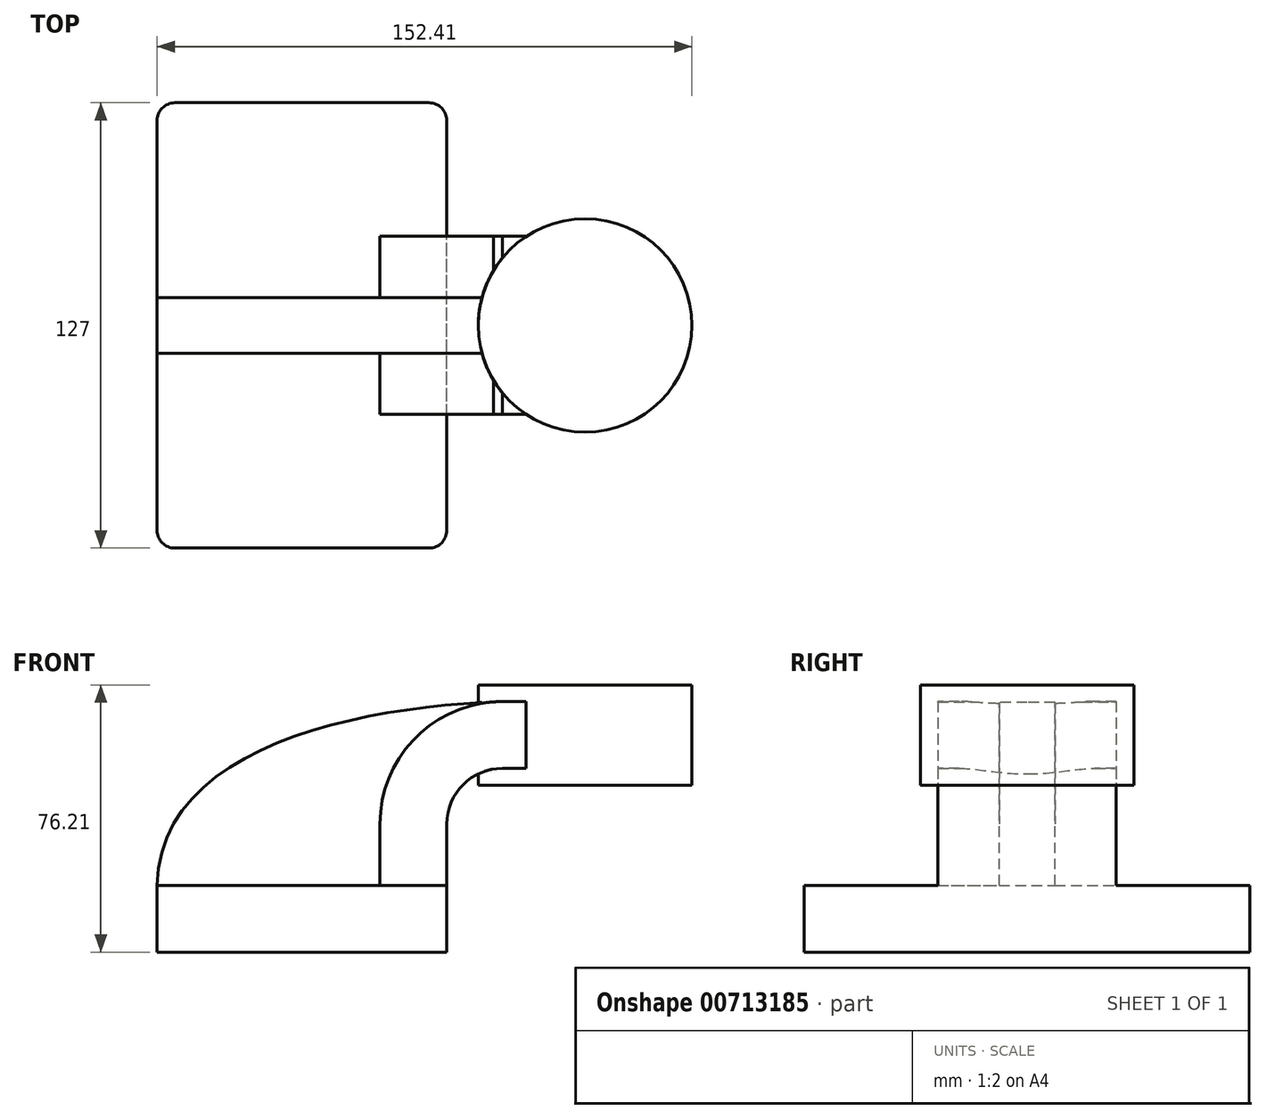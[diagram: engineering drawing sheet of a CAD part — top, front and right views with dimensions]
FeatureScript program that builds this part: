
annotation { "Feature Type Name" : "Feature", "Feature Type Description" : "" }
export const myFeature = defineFeature(function(context is Context, id is Id, definition is map)
    precondition{}
    {
        {
            var Q0;
            Q0=qCreatedBy(makeId("Front.planeOp"),FACE);
            var sketch = newSketch(context, id + "F0", { "sketchPlane" : qUnion([Q0])});
            skLineSegment(sketch, "E0.bottom", {"start": v(-41.28, 9.52) * mm, "end": v(41.28, 9.53) * mm});
            skLineSegment(sketch, "E0.top", {"start": v(-41.28, -9.53) * mm, "end": v(41.28, -9.53) * mm});
            skLineSegment(sketch, "E0.left", {"start": v(-41.28, 9.52) * mm, "end": v(-41.27, -9.53) * mm});
            skLineSegment(sketch, "E0.right", {"start": v(41.28, 9.53) * mm, "end": v(41.28, -9.52) * mm});
            skPoint(sketch, "E0.middle", {"position": v(0, 0) * mm});
            skLineSegment(sketch, "E1.bottom", {"start": v(111.12, 38.1) * mm, "end": v(60.33, 38.1) * mm});
            skLineSegment(sketch, "E1.top", {"start": v(111.12, 66.68) * mm, "end": v(60.33, 66.68) * mm});
            skLineSegment(sketch, "E1.left", {"start": v(111.12, 38.1) * mm, "end": v(111.12, 66.68) * mm});
            skLineSegment(sketch, "E1.right", {"start": v(60.33, 38.1) * mm, "end": v(60.33, 66.68) * mm});
            skPoint(sketch, "E1.middle", {"position": v(85.73, 52.39) * mm});
            skLineSegment(sketch, "E2", {"start": v(41.27, 9.53) * mm, "end": v(41.27, 27) * mm});
            skArc(sketch, "E3", {"start": v(57.15, 42.88) * mm, "mid": v(45.92, 38.23) * mm, "end": v(41.27, 27) * mm});
            skLineSegment(sketch, "E4", {"start": v(57.15, 42.88) * mm, "end": v(80.68, 42.88) * mm});
            skLineSegment(sketch, "E5.0", {"start": v(22.23, 9.53) * mm, "end": v(22.23, 27) * mm});
            skArc(sketch, "E5.1", {"start": v(57.15, 61.93) * mm, "mid": v(32.45, 51.7) * mm, "end": v(22.22, 27) * mm});
            skLineSegment(sketch, "E5.2", {"start": v(57.15, 61.93) * mm, "end": v(80.68, 61.93) * mm});
            skLineSegment(sketch, "E6", {"start": v(80.68, 38.1) * mm, "end": v(80.68, 66.68) * mm});
            skFitSpline(sketch, "E7", {"points": [v(-41.28, 9.53) * mm, v(57.15, 61.93) * mm], "startDerivative": vector(2.15, 119.8) * mm, "endDerivative": vector(119.5, 3.82) * mm});
            skSolve(sketch);
        }
        {
            var Q0;
            Q0=makeQuery(id+"F0.imprint","IMPRINT",FACE,{"disambiguationData":[TD([[makeQuery(id+"F0.imprint","IMPRINT",EDGE,{"derivedFrom":sQuery(id+"F0.wireOp",EDGE,"E0.top")}),1.0]])]});
            extrude(context, id + "F1", {"entities" : qUnion([Q0]), "endBound" : BoundingType.SYMMETRIC, "depth" : 127 * mm, "offsetDistance" : 25.4 * mm});
        }
        {
            var Q0;
            {var subQ1=sQuery(id+"F0.wireOp",EDGE,"E2");Q0=makeQuery(id+"F0.imprint","IMPRINT",FACE,{"disambiguationData":[TD([[makeQuery(id+"F0.imprint","IMPRINT",EDGE,{"derivedFrom":subQ1}),1.0]])]});}
            extrude(context, id + "F2", {"entities" : qUnion([Q0]), "operationType" : NewBodyOperationType.ADD, "endBound" : BoundingType.SYMMETRIC, "depth" : 50.8 * mm, "offsetDistance" : 25.4 * mm});
        }
        {
            var Q0;
            {var subQ3=sQuery(id+"F0.wireOp",EDGE,"E5.0");Q0=makeQuery(id+"F0.imprint","IMPRINT",FACE,{"disambiguationData":[TD([[makeQuery(id+"F0.imprint","IMPRINT",EDGE,{"derivedFrom":subQ3}),1.0]])]});}
            extrude(context, id + "F3", {"entities" : qUnion([Q0]), "operationType" : NewBodyOperationType.ADD, "endBound" : BoundingType.SYMMETRIC, "depth" : 15.88 * mm, "offsetDistance" : 25.4 * mm});
        }
        {
            var Q0;
            Q0=makeQuery(id+"F2.opExtrude","SWEPT_FACE",FACE,{"disambiguationData":[OSD([sQuery(id+"F0.wireOp",EDGE,"E1.right")])]});
            extrude(context, id + "F4", {"entities" : qUnion([Q0]), "operationType" : NewBodyOperationType.ADD, "depth" : 25.4 * mm, "offsetDistance" : 25.4 * mm});
        }
        {
            var Q0;
            {var subQ0=sQuery(id+"F0.wireOp",EDGE,"E1.left");Q0=makeQuery(id+"F0.imprint","IMPRINT",FACE,{"disambiguationData":[TD([[makeQuery(id+"F0.imprint","IMPRINT",EDGE,{"derivedFrom":subQ0}),1.0]])]});}
            var Q1;
            Q1=sQuery(id+"F0.wireOp",EDGE,"E6");
            revolve(context, id + "F5", {"operationType" : NewBodyOperationType.ADD, "surfaceOperationType" : NewSurfaceOperationType.NEW, "entities" : qUnion([Q0]), "axis" : qUnion([Q1]), "revolveType" : RevolveType.FULL});
        }
        {
            var Q0;
            Q0=makeQuery(id+"F1.opExtrude","CAP_EDGE",EDGE,{"disambiguationData":[OSD([sQuery(id+"F0.wireOp",EDGE,"E0.left")])],"isStart":true});
            var Q1;
            Q1=makeQuery(id+"F1.opExtrude","CAP_EDGE",EDGE,{"disambiguationData":[OSD([sQuery(id+"F0.wireOp",EDGE,"E0.left")])],"isStart":false});
            var Q2;
            Q2=makeQuery(id+"F1.opExtrude","CAP_EDGE",EDGE,{"disambiguationData":[OSD([sQuery(id+"F0.wireOp",EDGE,"E0.right")])],"isStart":true});
            var Q3;
            Q3=makeQuery(id+"F1.opExtrude","CAP_EDGE",EDGE,{"disambiguationData":[OSD([sQuery(id+"F0.wireOp",EDGE,"E0.right")])],"isStart":false});
            fillet(context, id + "F6", {"entities" : qUnion([Q0, Q1, Q2, Q3]), "radius" : 5.08 * mm, "tangentPropagation" : true, "allowEdgeOverflow" : false});
        }
    });
